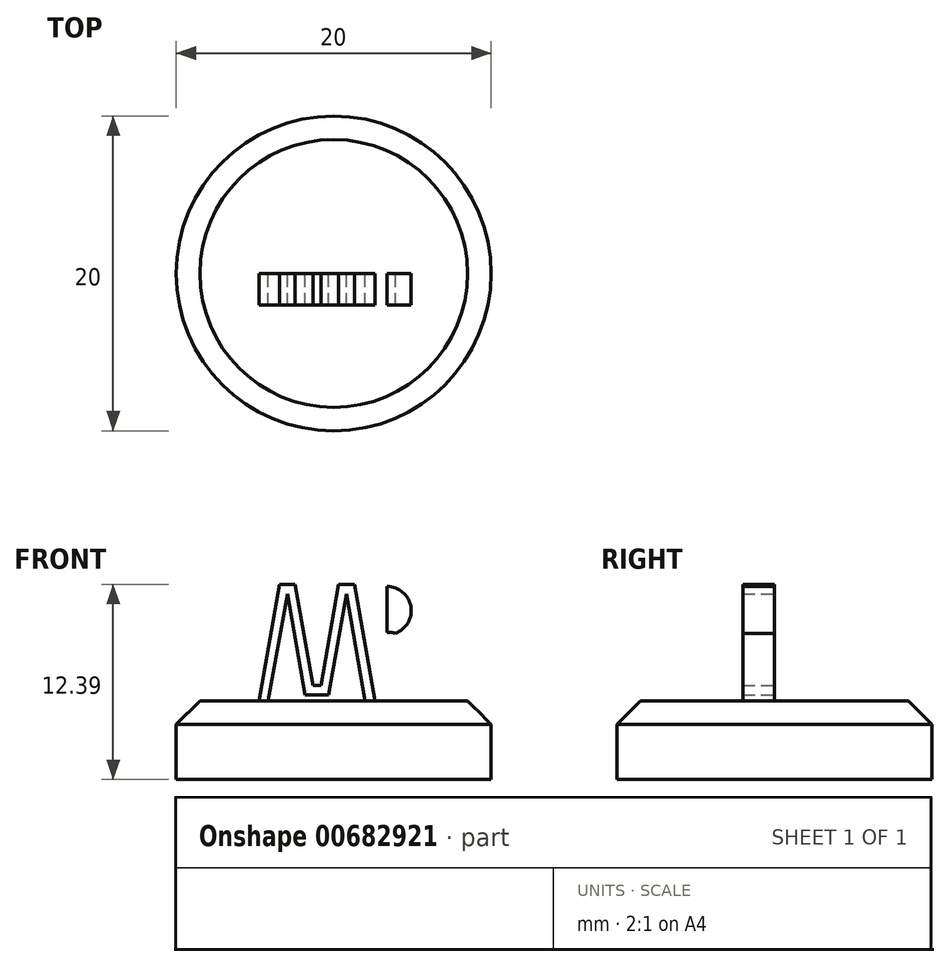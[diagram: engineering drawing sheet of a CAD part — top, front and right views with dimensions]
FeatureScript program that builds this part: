
annotation { "Feature Type Name" : "Feature", "Feature Type Description" : "" }
export const myFeature = defineFeature(function(context is Context, id is Id, definition is map)
    precondition{}
    {
        {
            var Q0;
            Q0=qCreatedBy(makeId("Top.planeOp"),FACE);
            var sketch = newSketch(context, id + "F0", { "sketchPlane" : qUnion([Q0])});
            skCircle(sketch, "E0", {"center": v(0, 0) * mm, "radius": 10 * mm});
            skSolve(sketch);
        }
        {
            var Q0;
            Q0=makeQuery(id+"F0.imprint","IMPRINT",FACE,{"disambiguationData":[TD([[makeQuery(id+"F0.imprint","IMPRINT",EDGE,{"derivedFrom":sQuery(id+"F0.wireOp",EDGE,"E0")}),1.0]])]});
            extrude(context, id + "F1", {"entities" : qUnion([Q0]), "depth" : 5 * mm, "offsetDistance" : 25 * mm});
        }
        {
            var Q0;
            Q0=makeQuery(id+"F1.opExtrude","CAP_EDGE",EDGE,{"disambiguationData":[OSD([sQuery(id+"F0.wireOp",EDGE,"E0")])],"isStart":false});
            chamfer(context, id + "F2", {"entities" : qUnion([Q0]), "width" : 1.5 * mm, "tangentPropagation" : true});
        }
        {
            var Q0;
            Q0=qCreatedBy(makeId("Front.planeOp"),FACE);
            var sketch = newSketch(context, id + "F3", { "sketchPlane" : qUnion([Q0])});
            skLineSegment(sketch, "E1", {"start": v(-4.75, 5) * mm, "end": v(-3.45, 12.39) * mm});
            skLineSegment(sketch, "E2", {"start": v(-3.45, 12.39) * mm, "end": v(-2.45, 12.39) * mm});
            skPoint(sketch, "E3.endSnap0", {"position": v(2.75, 2.5) * mm});
            skLineSegment(sketch, "E4", {"start": v(-2.45, 12.39) * mm, "end": v(-1.32, 5.98) * mm});
            skLineSegment(sketch, "E5", {"start": v(-1.32, 5.98) * mm, "end": v(-0.82, 5.98) * mm});
            skLineSegment(sketch, "E6", {"start": v(-0.82, 5.98) * mm, "end": v(0.3, 12.39) * mm});
            skLineSegment(sketch, "E7", {"start": v(0.3, 12.39) * mm, "end": v(1.3, 12.39) * mm});
            skLineSegment(sketch, "E8", {"start": v(1.3, 12.39) * mm, "end": v(2.61, 5) * mm});
            skLineSegment(sketch, "E9.1", {"start": v(0.8, 11.79) * mm, "end": v(0.81, 11.79) * mm});
            skLineSegment(sketch, "E9.4", {"start": v(-2.95, 11.79) * mm, "end": v(-2.94, 11.79) * mm});
            skLineSegment(sketch, "E9.6", {"start": v(-1.82, 5.38) * mm, "end": v(-0.32, 5.38) * mm});
            skLineSegment(sketch, "E10", {"start": v(-4.75, 5) * mm, "end": v(-4.16, 5) * mm});
            skLineSegment(sketch, "E11", {"start": v(3.4, 5.65) * mm, "end": v(3.4, 12.25) * mm});
            skLineSegment(sketch, "E12", {"start": v(3.4, 8.95) * mm, "end": v(3.4, 9.2) * mm});
            skLineSegment(sketch, "E13", {"start": v(3.4, 8.95) * mm, "end": v(3.4, 8.7) * mm});
            skLineSegment(sketch, "E14", {"start": v(3.4, 9.2) * mm, "end": v(3.4, 12.25) * mm});
            skLineSegment(sketch, "E15", {"start": v(3.4, 8.7) * mm, "end": v(3.4, 5.65) * mm});
            skArc(sketch, "E16", {"start": v(3.4, 12.25) * mm, "mid": v(4.92, 10.73) * mm, "end": v(3.4, 9.2) * mm});
            skArc(sketch, "E17", {"start": v(3.4, 8.7) * mm, "mid": v(4.93, 7.18) * mm, "end": v(3.4, 5.65) * mm});
            skArc(sketch, "E18.0", {"start": v(3.38, 12.9) * mm, "mid": v(5.57, 10.73) * mm, "end": v(3.4, 8.55) * mm});
            skArc(sketch, "E19.0", {"start": v(3.4, 9.35) * mm, "mid": v(5.58, 7.17) * mm, "end": v(3.4, 5) * mm});
            skLineSegment(sketch, "E20.0", {"start": v(2.75, 5.65) * mm, "end": v(2.75, 12.25) * mm});
            skLineSegment(sketch, "E21", {"start": v(3.38, 12.9) * mm, "end": v(2.75, 12.9) * mm});
            skLineSegment(sketch, "E22", {"start": v(2.75, 12.9) * mm, "end": v(2.75, 12.25) * mm});
            skLineSegment(sketch, "E23", {"start": v(3.4, 5) * mm, "end": v(2.75, 5) * mm});
            skLineSegment(sketch, "E24", {"start": v(2.75, 5) * mm, "end": v(2.75, 5.65) * mm});
            skLineSegment(sketch, "E25", {"start": v(2, 5) * mm, "end": v(2.61, 5) * mm});
            skLineSegment(sketch, "E26", {"start": v(-2.94, 11.79) * mm, "end": v(-4.16, 5) * mm});
            skLineSegment(sketch, "E27", {"start": v(0.81, 11.79) * mm, "end": v(2, 5) * mm});
            skLineSegment(sketch, "E28", {"start": v(0.81, 11.79) * mm, "end": v(-0.32, 5.38) * mm});
            skLineSegment(sketch, "E29", {"start": v(-2.94, 11.79) * mm, "end": v(-1.82, 5.38) * mm});
            skSolve(sketch);
        }
        {
            var Q0;
            {var subQ5=sQuery(id+"F3.wireOp",EDGE,"E12");Q0=makeQuery(id+"F3.imprint","IMPRINT",FACE,{"disambiguationData":[TD([[makeQuery(id+"F3.imprint","IMPRINT",EDGE,{"derivedFrom":subQ5}),-1.0]])]});}
            var Q1;
            {var subQ1=sQuery(id+"F3.wireOp",EDGE,"E14");var subQ3=sQuery(id+"F3.wireOp",EDGE,"E19.0");var subQ4=makeQuery(id+"F3.imprint","INTERSECT",VERTEX,{"derivedFrom":[subQ1,subQ3]});Q1=makeQuery(id+"F3.imprint","IMPRINT",FACE,{"disambiguationData":[TD([[makeQuery(id+"F3.imprint","IMPRINT",EDGE,{"disambiguationData":[TD([[subQ4,-1.0]])],"derivedFrom":subQ3}),-1.0]])]});}
            var Q2;
            {var subQ14=sQuery(id+"F3.wireOp",EDGE,"E12");Q2=makeQuery(id+"F3.imprint","IMPRINT",FACE,{"disambiguationData":[TD([[makeQuery(id+"F3.imprint","IMPRINT",EDGE,{"derivedFrom":subQ14}),1.0]])]});}
            extrude(context, id + "F4", {"entities" : qUnion([Q0, Q1, Q2]), "operationType" : NewBodyOperationType.ADD, "depth" : 2 * mm, "offsetDistance" : 25 * mm});
        }
        {
            var Q0;
            Q0=makeQuery(id+"F3.imprint","IMPRINT",FACE,{"disambiguationData":[TD([[makeQuery(id+"F3.imprint","IMPRINT",EDGE,{"derivedFrom":sQuery(id+"F3.wireOp",EDGE,"E1")}),-1.0]])]});
            extrude(context, id + "F5", {"entities" : qUnion([Q0]), "depth" : 2 * mm, "offsetDistance" : 25 * mm});
        }
    });
